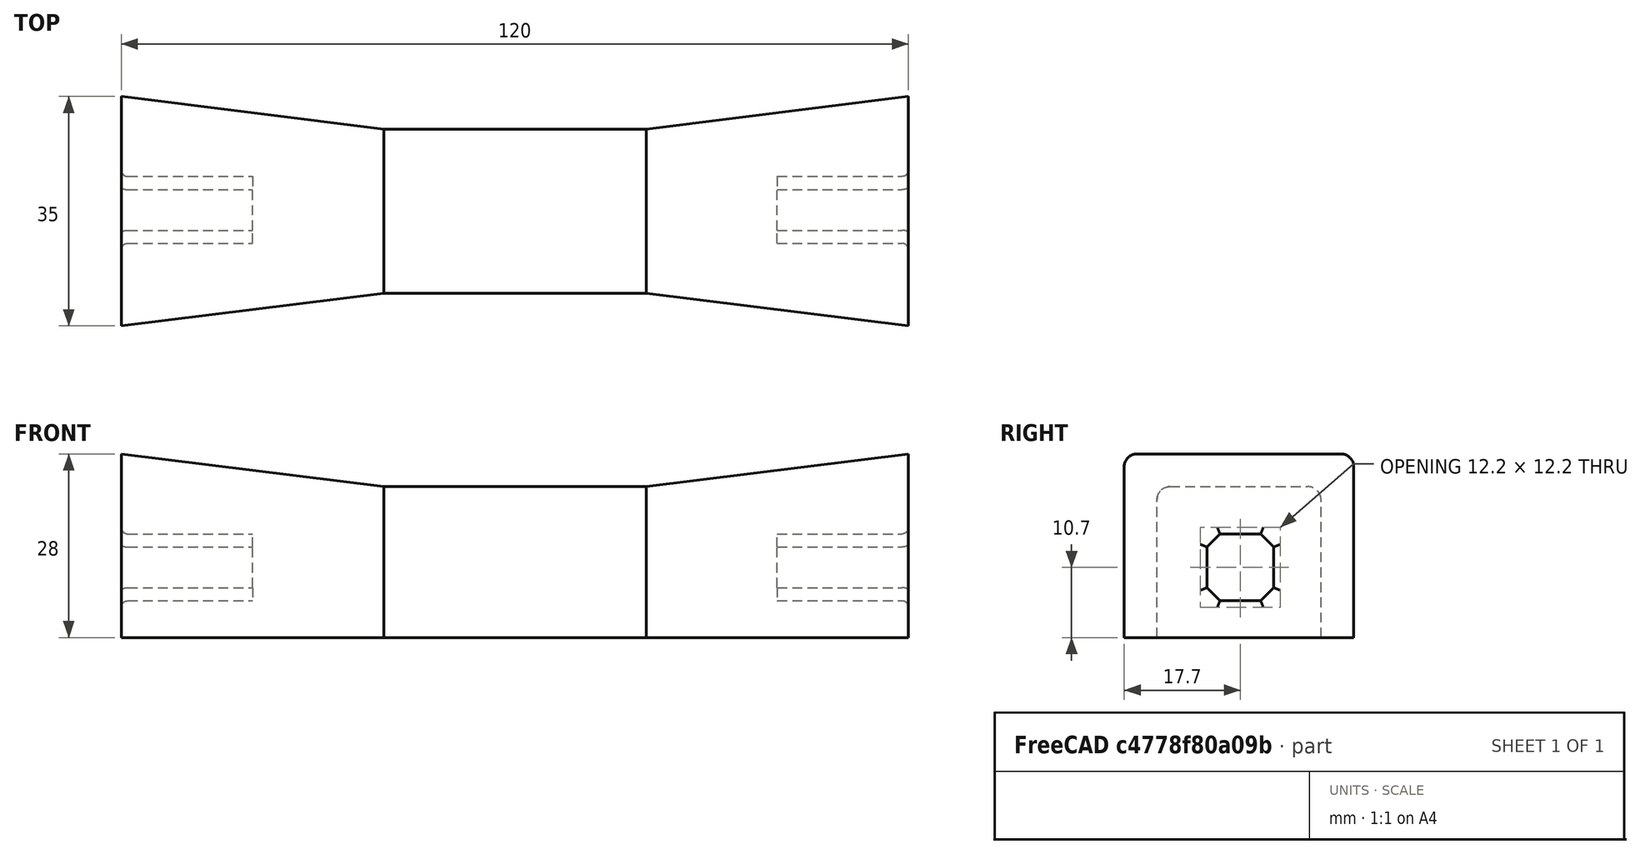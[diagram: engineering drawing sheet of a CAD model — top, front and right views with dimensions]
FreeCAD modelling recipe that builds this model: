
FCSTD DOCUMENT  (FreeCAD 0.14R3703 (Git))
Label: Roller_Bridge
License: CC-BY 3.0
LicenseURL: http://creativecommons.org/licenses/by/3.0/
objects: Part::Box×4, Part::Fillet×4, Part::Cut×3, Part::Wedge×2, Part::Chamfer×2, Part::MultiFuse×1
note: 16 computed .brp shape members not serialized (recipe doc carries the construction recipe); baked Part::Feature solids carry a one-line shape summary decoded from their .brp

FEATURE [Part::Box] Box  label="Cube"
  Height = 25
  Length = 40
  Width = 25
FEATURE [Part::Fillet] Fillet  label="Middle"
  Base = -> Box
  Edges = 4 edges r=2: [Edge9,Edge10,Edge11,Edge12]
FEATURE [Part::Wedge] Wedge
  Placement = pos=(-40,-40,-5) rot=(0,0,1;0rad)
  X2max = 30
  X2min = 5
  Xmax = 35
  Xmin = 0
  Ymax = 40
  Ymin = 0
  Z2max = 30
  Z2min = 5
  Zmax = 35
  Zmin = 0
FEATURE [Part::Fillet] Fillet001  label="Left"
  Base = -> Wedge
  Edges = 4 edges r=2: [Edge2,Edge4,Edge6,Edge8]
  Placement = pos=(0,-10,0) rot=(0,0,-1;1.5708rad)
FEATURE [Part::Wedge] Wedge001
  Placement = pos=(-40,-40,-5) rot=(0,0,1;0rad)
  X2max = 30
  X2min = 5
  Xmax = 35
  Xmin = 0
  Ymax = 40
  Ymin = 0
  Z2max = 30
  Z2min = 5
  Zmax = 35
  Zmin = 0
FEATURE [Part::Fillet] Fillet002  label="Right"
  Base = -> Wedge001
  Edges = 4 edges r=2: [Edge2,Edge4,Edge6,Edge8]
  Placement = pos=(40,35,0) rot=(0,0,1;1.5708rad)
FEATURE [Part::Box] Box001  label="Cube001"
  Height = 10.2
  Length = 20
  Width = 10.2
FEATURE [Part::Chamfer] Chamfer  label="Connector-hole2"
  Base = -> Box001
  Edges = 4 edges r=2: [Edge9,Edge10,Edge11,Edge12]
  Placement = pos=(60,7.6,7.6) rot=(0,0,1;0rad)
FEATURE [Part::Box] Box002  label="Cube002"
  Height = 10.2
  Length = 20
  Width = 10.2
FEATURE [Part::Chamfer] Chamfer001  label="Connector-hole1"
  Base = -> Box002
  Edges = 4 edges r=2: [Edge9,Edge10,Edge11,Edge12]
  Placement = pos=(-40,7.6,7.6) rot=(0,0,1;0rad)
FEATURE [Part::Box] Box003  label="Cut-bottom"
  Height = 12
  Length = 140
  Placement = pos=(-50,-50,-10) rot=(0,0,1;0rad)
  Width = 140
FEATURE [Part::MultiFuse] Fusion  label="Base"
  Shapes = -> [Fillet001,Fillet002,Fillet]
FEATURE [Part::Cut] Cut
  Base = -> Fusion
  Tool = -> Chamfer001
FEATURE [Part::Cut] Cut001
  Base = -> Cut
  Tool = -> Chamfer
FEATURE [Part::Cut] Cut002
  Base = -> Cut001
  Tool = -> Box003
FEATURE [Part::Fillet] Fillet003  label="Roller-Bridge"
  Base = -> Cut002
  Edges = 16 edges r=1: [Edge7,Edge8,Edge9,Edge10,Edge11,Edge12,Edge13,Edge14,Edge60,Edge61,Edge62,Edge63,Edge64,Edge65,Edge66,Edge67]
